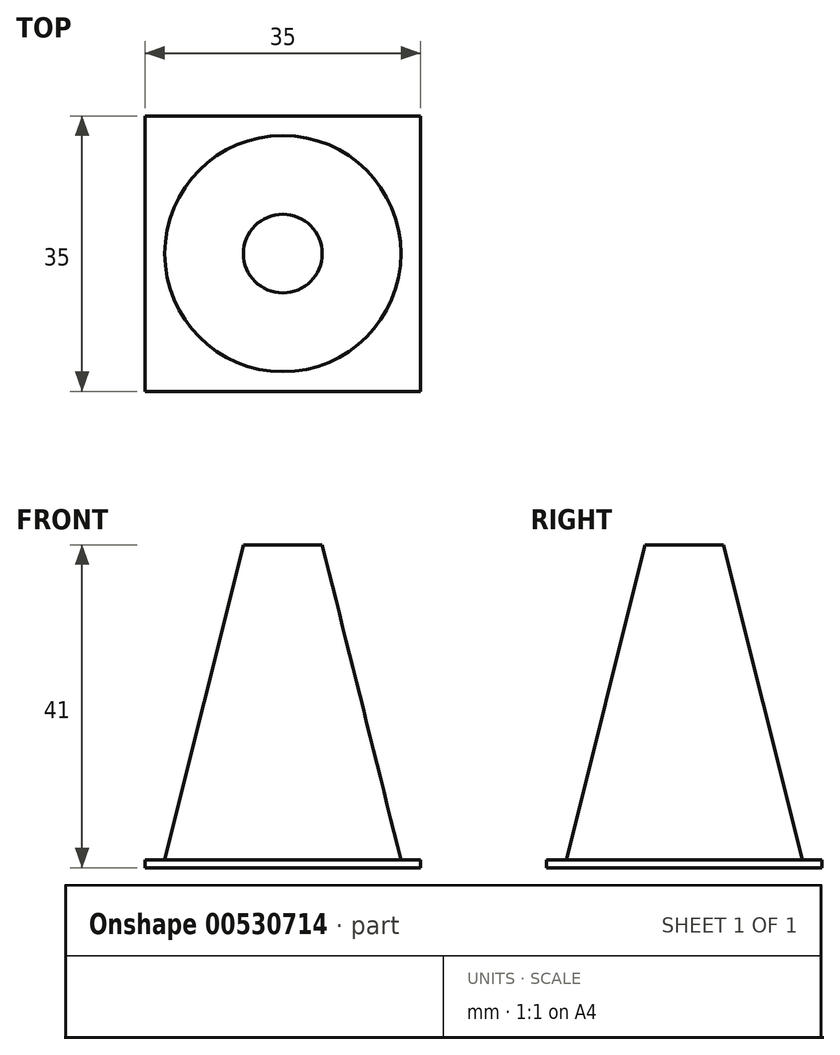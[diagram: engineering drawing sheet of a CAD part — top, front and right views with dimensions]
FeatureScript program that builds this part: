
annotation { "Feature Type Name" : "Feature", "Feature Type Description" : "" }
export const myFeature = defineFeature(function(context is Context, id is Id, definition is map)
    precondition{}
    {
        {
            var Q0;
            Q0=qCreatedBy(makeId("Top.planeOp"),FACE);
            var sketch = newSketch(context, id + "F0", { "sketchPlane" : qUnion([Q0])});
            skCircle(sketch, "E0", {"center": v(0, 0) * mm, "radius": 15 * mm});
            skSolve(sketch);
        }
        {
            var Q0;
            Q0=qCreatedBy(makeId("Top.planeOp"),FACE);
            cPlane(context, id + "F1", {"entities" : qUnion([Q0]), "cplaneType" : CPlaneType.OFFSET, "offset" : 10 * mm, "width" : 152.4 * mm, "height" : 152.4 * mm});
        }
        {
            var Q0;
            Q0=qCreatedBy(id+"F1.planeOp",FACE);
            var sketch = newSketch(context, id + "F2", { "sketchPlane" : qUnion([Q0])});
            skCircle(sketch, "E1", {"center": v(0, 0) * mm, "radius": 12.5 * mm});
            skSolve(sketch);
        }
        {
            var Q0;
            Q0=qCreatedBy(id+"F1.planeOp",FACE);
            cPlane(context, id + "F3", {"entities" : qUnion([Q0]), "cplaneType" : CPlaneType.OFFSET, "offset" : 10 * mm, "width" : 152.4 * mm, "height" : 152.4 * mm});
        }
        {
            var Q0;
            Q0=qCreatedBy(id+"F3.planeOp",FACE);
            var sketch = newSketch(context, id + "F4", { "sketchPlane" : qUnion([Q0])});
            skCircle(sketch, "E2", {"center": v(0, 0) * mm, "radius": 10 * mm});
            skSolve(sketch);
        }
        {
            var Q0;
            Q0=qCreatedBy(id+"F3.planeOp",FACE);
            cPlane(context, id + "F5", {"entities" : qUnion([Q0]), "cplaneType" : CPlaneType.OFFSET, "offset" : 10 * mm, "width" : 152.4 * mm, "height" : 152.4 * mm});
        }
        {
            var Q0;
            Q0=qCreatedBy(id+"F5.planeOp",FACE);
            var sketch = newSketch(context, id + "F6", { "sketchPlane" : qUnion([Q0])});
            skCircle(sketch, "E3", {"center": v(0, 0) * mm, "radius": 7.5 * mm});
            skSolve(sketch);
        }
        {
            var Q0;
            Q0=qCreatedBy(id+"F5.planeOp",FACE);
            cPlane(context, id + "F7", {"entities" : qUnion([Q0]), "cplaneType" : CPlaneType.OFFSET, "offset" : 10 * mm, "width" : 152.4 * mm, "height" : 152.4 * mm});
        }
        {
            var Q0;
            Q0=qCreatedBy(id+"F7.planeOp",FACE);
            var sketch = newSketch(context, id + "F8", { "sketchPlane" : qUnion([Q0])});
            skCircle(sketch, "E4", {"center": v(0, 0) * mm, "radius": 5 * mm});
            skSolve(sketch);
        }
        {
            var Q0;
            Q0 = qSketchRegion(id + "F0", true);
            var Q1;
            Q1 = qSketchRegion(id + "F2", true);
            var Q2;
            Q2 = qSketchRegion(id + "F4", true);
            var Q3;
            Q3 = qSketchRegion(id + "F6", true);
            var Q4;
            Q4 = qSketchRegion(id + "F8", true);
            loft(context, id + "F9", {"sheetProfilesArray" : [{ "sheetProfileEntities" : qUnion([Q0]) }, { "sheetProfileEntities" : qUnion([Q1]) }, { "sheetProfileEntities" : qUnion([Q2]) }, { "sheetProfileEntities" : qUnion([Q3]) }, { "sheetProfileEntities" : qUnion([Q4]) }]});
        }
        {
            var Q0;
            Q0=qCreatedBy(makeId("Top.planeOp"),FACE);
            var sketch = newSketch(context, id + "F10", { "sketchPlane" : qUnion([Q0])});
            skLineSegment(sketch, "E5.bottom", {"start": v(17.5, -17.5) * mm, "end": v(-17.5, -17.5) * mm});
            skLineSegment(sketch, "E5.top", {"start": v(17.5, 17.5) * mm, "end": v(-17.5, 17.5) * mm});
            skLineSegment(sketch, "E5.left", {"start": v(17.5, -17.5) * mm, "end": v(17.5, 17.5) * mm});
            skLineSegment(sketch, "E5.right", {"start": v(-17.5, -17.5) * mm, "end": v(-17.5, 17.5) * mm});
            skPoint(sketch, "E5.middle", {"position": v(0, 0) * mm});
            skSolve(sketch);
        }
        {
            var Q0;
            Q0 = qSketchRegion(id + "F10", true);
            extrude(context, id + "F11", {"entities" : qUnion([Q0]), "operationType" : NewBodyOperationType.ADD, "oppositeDirection" : true, "depth" : 1 * mm, "offsetDistance" : 25.4 * mm});
        }
    });
